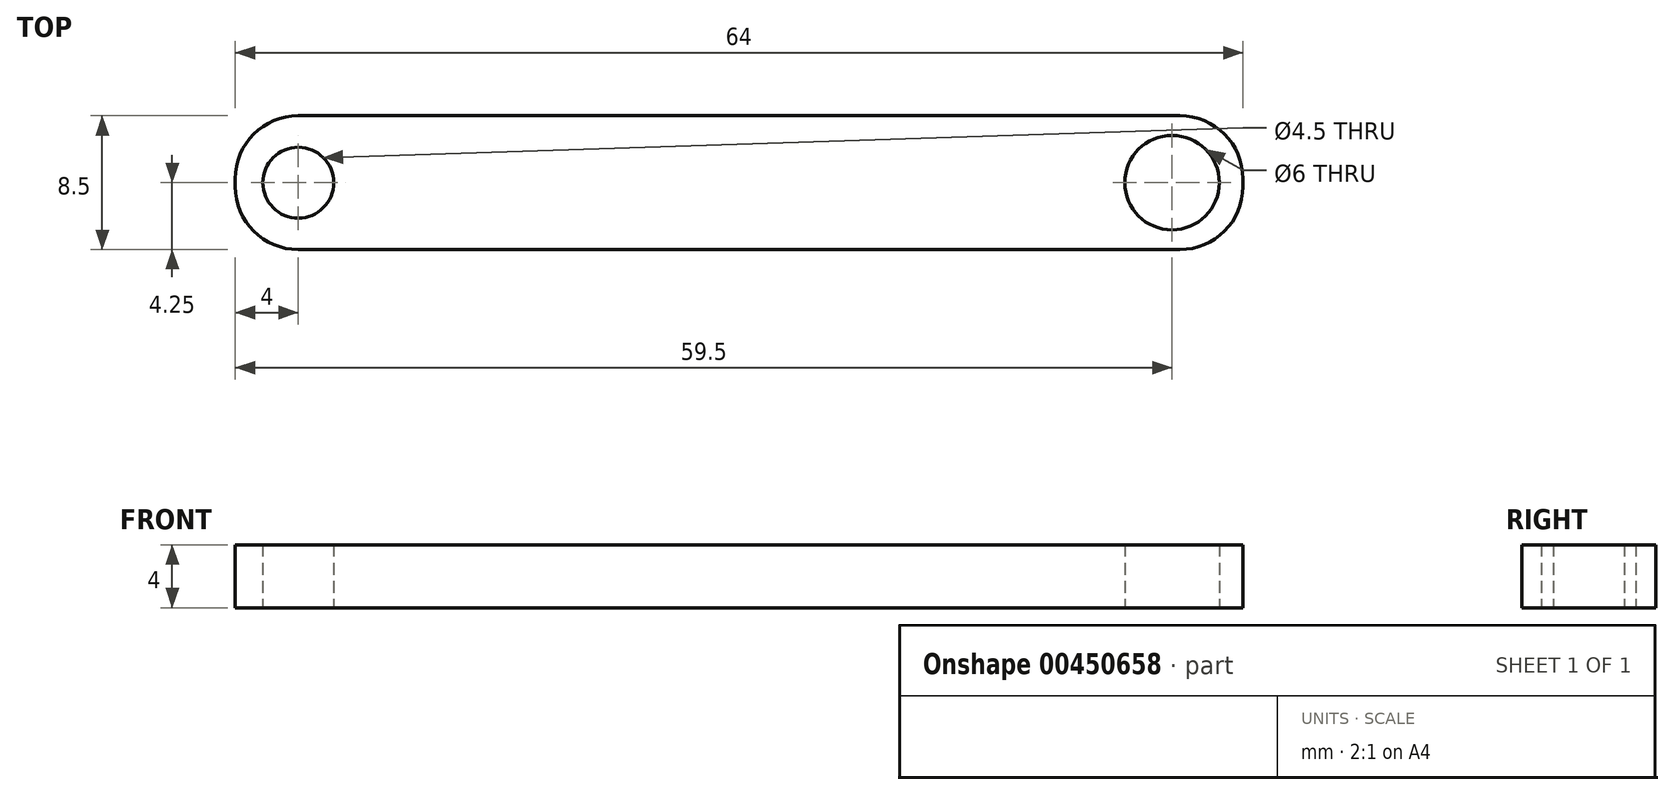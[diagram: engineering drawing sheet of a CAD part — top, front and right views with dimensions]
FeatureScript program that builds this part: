
annotation { "Feature Type Name" : "Feature", "Feature Type Description" : "" }
export const myFeature = defineFeature(function(context is Context, id is Id, definition is map)
    precondition{}
    {
        {
            var Q0;
            Q0=qCreatedBy(makeId("Top.planeOp"),FACE);
            var sketch = newSketch(context, id + "F0", { "sketchPlane" : qUnion([Q0])});
            skLineSegment(sketch, "E0.bottom", {"start": v(32, 4.25) * mm, "end": v(-32, 4.25) * mm});
            skLineSegment(sketch, "E0.top", {"start": v(32, -4.25) * mm, "end": v(-32, -4.25) * mm});
            skLineSegment(sketch, "E0.left", {"start": v(32, 4.25) * mm, "end": v(32, -4.25) * mm});
            skLineSegment(sketch, "E0.right", {"start": v(-32, 4.25) * mm, "end": v(-32, -4.25) * mm});
            skPoint(sketch, "E0.middle", {"position": v(0, 0) * mm});
            skCircle(sketch, "E1", {"center": v(-28, 0) * mm, "radius": 2.25 * mm});
            skCircle(sketch, "E2", {"center": v(27.5, 0) * mm, "radius": 3 * mm});
            skSolve(sketch);
        }
        {
            var Q0;
            Q0 = qSketchRegion(id + "F0", true);
            extrude(context, id + "F1", {"entities" : qUnion([Q0]), "endBound" : BoundingType.SYMMETRIC, "depth" : 4 * mm});
        }
        {
            var Q0;
            Q0=makeQuery(id+"F1.opExtrude","SWEPT_EDGE",EDGE,{"disambiguationData":[OSD([sQuery(id+"F0.wireOp",EDGE,"E0.bottom"),sQuery(id+"F0.wireOp",EDGE,"E0.right")])]});
            var Q1;
            Q1=makeQuery(id+"F1.opExtrude","SWEPT_EDGE",EDGE,{"disambiguationData":[OSD([sQuery(id+"F0.wireOp",EDGE,"E0.top"),sQuery(id+"F0.wireOp",EDGE,"E0.right")])]});
            var Q2;
            Q2=makeQuery(id+"F1.opExtrude","SWEPT_EDGE",EDGE,{"disambiguationData":[OSD([sQuery(id+"F0.wireOp",EDGE,"E0.bottom"),sQuery(id+"F0.wireOp",EDGE,"E0.left")])]});
            var Q3;
            Q3=makeQuery(id+"F1.opExtrude","SWEPT_EDGE",EDGE,{"disambiguationData":[OSD([sQuery(id+"F0.wireOp",EDGE,"E0.top"),sQuery(id+"F0.wireOp",EDGE,"E0.left")])]});
            fillet(context, id + "F2", {"entities" : qUnion([Q0, Q1, Q2, Q3]), "radius" : 4 * mm, "tangentPropagation" : true, "allowEdgeOverflow" : false});
        }
    });
